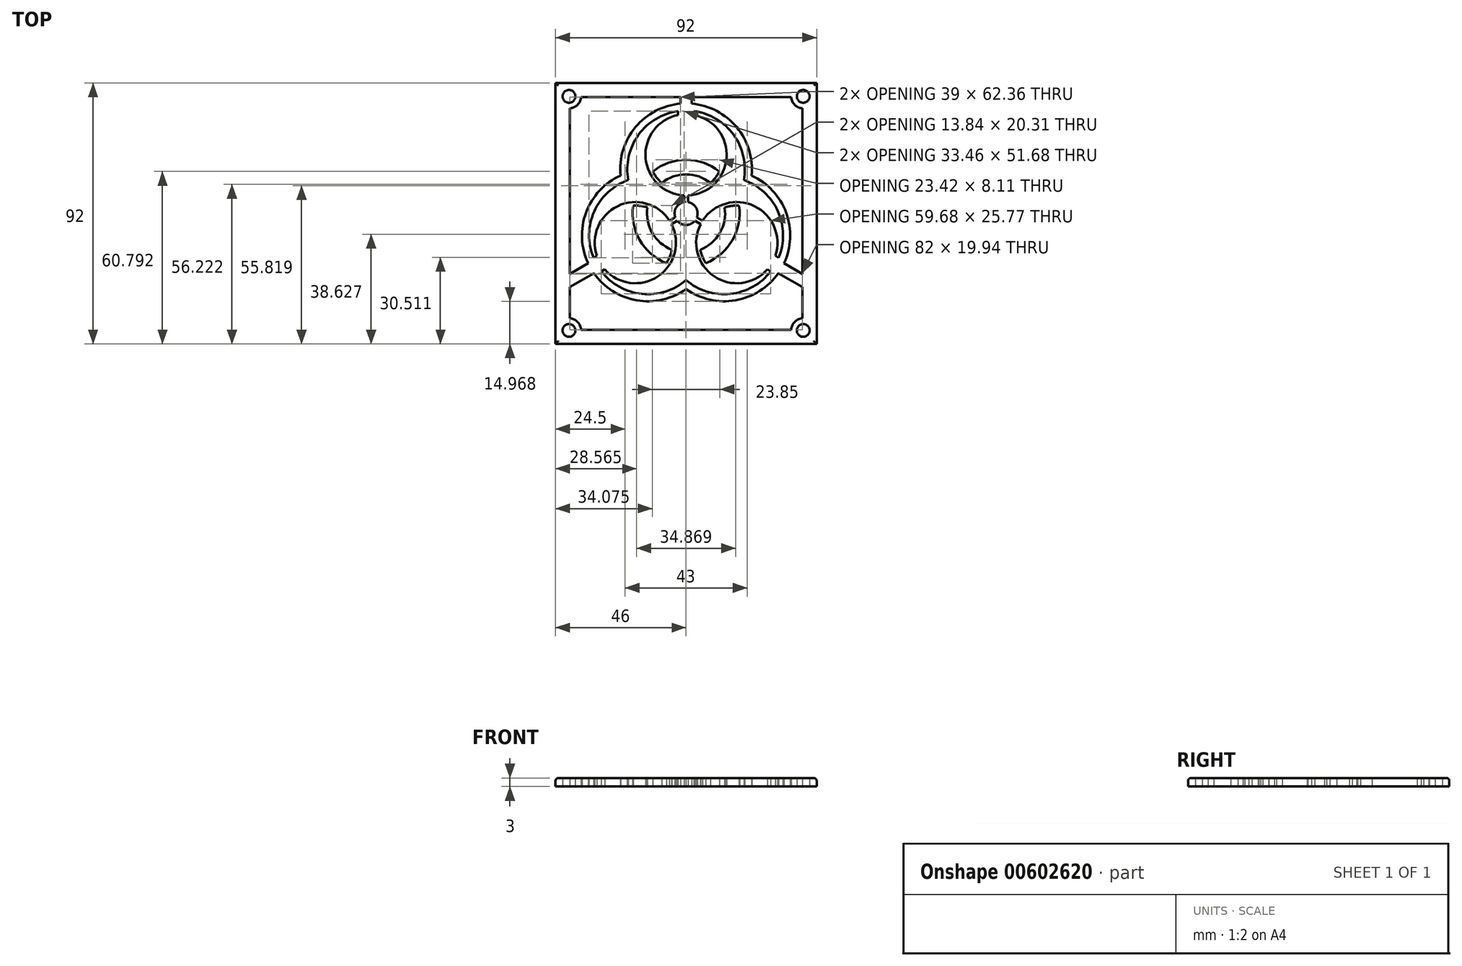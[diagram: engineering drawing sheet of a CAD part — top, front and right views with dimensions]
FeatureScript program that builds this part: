
annotation { "Feature Type Name" : "Feature", "Feature Type Description" : "" }
export const myFeature = defineFeature(function(context is Context, id is Id, definition is map)
    precondition{}
    {
        {
            var Q0;
            Q0=qCreatedBy(makeId("Top.planeOp"),FACE);
            var sketch = newSketch(context, id + "F0", { "sketchPlane" : qUnion([Q0])});
            skPoint(sketch, "E0.middle", {"position": v(0, 0) * mm});
            skLineSegment(sketch, "E1.bottom", {"start": v(46, 46) * mm, "end": v(-46, 46) * mm});
            skLineSegment(sketch, "E1.top", {"start": v(46, -46) * mm, "end": v(-46, -46) * mm});
            skLineSegment(sketch, "E1.left", {"start": v(46, 46) * mm, "end": v(46, -46) * mm});
            skLineSegment(sketch, "E1.right", {"start": v(-46, 46) * mm, "end": v(-46, -46) * mm});
            skCircle(sketch, "E2", {"center": v(-41.25, 41.25) * mm, "radius": 2.25 * mm});
            skCircle(sketch, "E3", {"center": v(41.25, 41.25) * mm, "radius": 2.25 * mm});
            skCircle(sketch, "E4", {"center": v(-41.25, -41.25) * mm, "radius": 2.25 * mm});
            skCircle(sketch, "E5", {"center": v(41.25, -41.25) * mm, "radius": 2.25 * mm});
            skArc(sketch, "E6", {"start": v(-0.7, 4) * mm, "mid": v(-3.51, 2.03) * mm, "end": v(-3.8, -1.39) * mm});
            skArc(sketch, "E7", {"start": v(0.7, 6.34) * mm, "mid": v(14.26, 19.58) * mm, "end": v(2.79, 34.66) * mm});
            skArc(sketch, "E8.1.0", {"start": v(-5.84, -2.56) * mm, "mid": v(-24.09, 2.57) * mm, "end": v(-31.4, -14.91) * mm});
            skArc(sketch, "E8.2.0", {"start": v(5.14, -3.78) * mm, "mid": v(9.82, -22.14) * mm, "end": v(28.62, -19.74) * mm});
            skArc(sketch, "E9", {"start": v(11.71, 14.77) * mm, "mid": v(0, 18.85) * mm, "end": v(-11.71, 14.77) * mm});
            skArc(sketch, "E10", {"start": v(8.58, 10.74) * mm, "mid": v(0, 13.75) * mm, "end": v(-8.58, 10.74) * mm});
            skArc(sketch, "E11.trimOffspring", {"start": v(-20.35, 11.75) * mm, "mid": v(-32.36, 0.7) * mm, "end": v(-32.63, -15.62) * mm});
            skArc(sketch, "E12.trimOffspring", {"start": v(20.35, 11.75) * mm, "mid": v(16.78, 27.67) * mm, "end": v(2.79, 36.06) * mm});
            skArc(sketch, "E13.trimOffspring", {"start": v(-18.65, 2.76) * mm, "mid": v(-16.32, -9.42) * mm, "end": v(-6.93, -17.53) * mm});
            skArc(sketch, "E14.trimOffspring", {"start": v(-13.59, 2.07) * mm, "mid": v(-11.9, -6.87) * mm, "end": v(-5, -12.8) * mm});
            skArc(sketch, "E15.trimOffspring", {"start": v(0, -23.5) * mm, "mid": v(15.57, -28.37) * mm, "end": v(29.84, -20.45) * mm});
            skArc(sketch, "E16.trimOffspring", {"start": v(6.93, -17.53) * mm, "mid": v(16.32, -9.42) * mm, "end": v(18.65, 2.76) * mm});
            skArc(sketch, "E17.trimOffspring", {"start": v(5, -12.8) * mm, "mid": v(11.9, -6.87) * mm, "end": v(13.59, 2.07) * mm});
            skArc(sketch, "E18.0", {"start": v(-11.71, 14.77) * mm, "mid": v(-10.35, 12.6) * mm, "end": v(-8.58, 10.74) * mm});
            skArc(sketch, "E19.1.0", {"start": v(-13.59, 2.07) * mm, "mid": v(-16.08, 2.66) * mm, "end": v(-18.65, 2.76) * mm});
            skArc(sketch, "E19.2.0", {"start": v(5, -12.8) * mm, "mid": v(5.74, -15.26) * mm, "end": v(6.93, -17.53) * mm});
            skArc(sketch, "E20.trimOffspring", {"start": v(8.58, 10.74) * mm, "mid": v(10.35, 12.6) * mm, "end": v(11.71, 14.77) * mm});
            skArc(sketch, "E21.trimOffspring", {"start": v(18.65, 2.76) * mm, "mid": v(16.08, 2.66) * mm, "end": v(13.59, 2.07) * mm});
            skArc(sketch, "E22.trimOffspring", {"start": v(-6.93, -17.53) * mm, "mid": v(-5.74, -15.26) * mm, "end": v(-5, -12.8) * mm});
            skLineSegment(sketch, "E23.left", {"start": v(-0.7, 6.34) * mm, "end": v(-0.7, 4) * mm});
            skLineSegment(sketch, "E23.right", {"start": v(0.7, 6.34) * mm, "end": v(0.7, 4) * mm});
            skLineSegment(sketch, "E24.left", {"start": v(-2.79, 36.06) * mm, "end": v(-2.79, 34.66) * mm});
            skLineSegment(sketch, "E24.right", {"start": v(2.79, 36.06) * mm, "end": v(2.79, 34.66) * mm});
            skArc(sketch, "E25.trimOffspring", {"start": v(-2.79, 36.06) * mm, "mid": v(-16.78, 27.67) * mm, "end": v(-20.35, 11.75) * mm});
            skArc(sketch, "E26.trimOffspring", {"start": v(-2.79, 34.66) * mm, "mid": v(-14.26, 19.58) * mm, "end": v(-0.7, 6.34) * mm});
            skLineSegment(sketch, "E27.1.0", {"start": v(-29.84, -20.45) * mm, "end": v(-28.62, -19.74) * mm});
            skLineSegment(sketch, "E27.1.1", {"start": v(-32.63, -15.62) * mm, "end": v(-31.4, -14.91) * mm});
            skLineSegment(sketch, "E27.1.2", {"start": v(-5.14, -3.78) * mm, "end": v(-3.1, -2.6) * mm});
            skLineSegment(sketch, "E27.1.3", {"start": v(-5.84, -2.56) * mm, "end": v(-3.8, -1.39) * mm});
            skLineSegment(sketch, "E27.2.0", {"start": v(32.63, -15.62) * mm, "end": v(31.4, -14.91) * mm});
            skLineSegment(sketch, "E27.2.1", {"start": v(29.84, -20.45) * mm, "end": v(28.62, -19.74) * mm});
            skLineSegment(sketch, "E27.2.2", {"start": v(5.84, -2.56) * mm, "end": v(3.8, -1.39) * mm});
            skLineSegment(sketch, "E27.2.3", {"start": v(5.14, -3.78) * mm, "end": v(3.1, -2.6) * mm});
            skArc(sketch, "E28.trimOffspring", {"start": v(3.8, -1.39) * mm, "mid": v(3.51, 2.03) * mm, "end": v(0.7, 4) * mm});
            skArc(sketch, "E29.trimOffspring", {"start": v(-3.1, -2.6) * mm, "mid": v(0, -4.05) * mm, "end": v(3.1, -2.6) * mm});
            skArc(sketch, "E30.trimOffspring", {"start": v(32.63, -15.62) * mm, "mid": v(32.36, 0.7) * mm, "end": v(20.35, 11.75) * mm});
            skArc(sketch, "E31.trimOffspring", {"start": v(31.4, -14.91) * mm, "mid": v(24.09, 2.57) * mm, "end": v(5.84, -2.56) * mm});
            skArc(sketch, "E32.trimOffspring", {"start": v(-29.84, -20.45) * mm, "mid": v(-15.57, -28.37) * mm, "end": v(0, -23.5) * mm});
            skArc(sketch, "E33.trimOffspring", {"start": v(-28.62, -19.74) * mm, "mid": v(-9.82, -22.14) * mm, "end": v(-5.14, -3.78) * mm});
            skArc(sketch, "E34.0", {"start": v(-3.12, 38.54) * mm, "mid": v(-18.19, 29.96) * mm, "end": v(-23.1, 13.34) * mm});
            skArc(sketch, "E35.0", {"start": v(-23.1, 13.34) * mm, "mid": v(-35.24, 0.24) * mm, "end": v(-34.49, -17.6) * mm});
            skArc(sketch, "E36.0", {"start": v(-31.82, -21.98) * mm, "mid": v(-16.85, -30.73) * mm, "end": v(0, -26.67) * mm});
            skArc(sketch, "E37.0", {"start": v(0, -26.67) * mm, "mid": v(17.41, -30.64) * mm, "end": v(32.49, -21.06) * mm});
            skArc(sketch, "E38.0", {"start": v(34.94, -16.56) * mm, "mid": v(35.04, 0.77) * mm, "end": v(23.1, 13.34) * mm});
            skArc(sketch, "E39.0", {"start": v(23.1, 13.34) * mm, "mid": v(17.83, 30.4) * mm, "end": v(2, 38.67) * mm});
            skLineSegment(sketch, "E40.1", {"start": v(41, 37) * mm, "end": v(41, -21.36) * mm});
            skLineSegment(sketch, "E40.2", {"start": v(41, -41) * mm, "end": v(39.01, -41) * mm});
            skLineSegment(sketch, "E40.3", {"start": v(-41, 39.01) * mm, "end": v(-41, -21.36) * mm});
            skArc(sketch, "E41.0", {"start": v(-41, 37) * mm, "mid": v(-38.24, 38.24) * mm, "end": v(-37, 41) * mm});
            skArc(sketch, "E42.1.0", {"start": v(-37, -41) * mm, "mid": v(-38.24, -38.24) * mm, "end": v(-41, -37) * mm});
            skArc(sketch, "E42.2.0", {"start": v(41, -37) * mm, "mid": v(38.24, -38.24) * mm, "end": v(37, -41) * mm});
            skArc(sketch, "E42.3.0", {"start": v(37, 41) * mm, "mid": v(38.24, 38.24) * mm, "end": v(41, 37) * mm});
            skLineSegment(sketch, "E43.trimOffspring", {"start": v(37, 41) * mm, "end": v(2, 41) * mm});
            skLineSegment(sketch, "E44.trimOffspring", {"start": v(37, -41) * mm, "end": v(-37, -41) * mm});
            skLineSegment(sketch, "E45.0", {"start": v(-2, 38.67) * mm, "end": v(-2, 41) * mm});
            skLineSegment(sketch, "E46.0", {"start": v(2, 38.67) * mm, "end": v(2, 41) * mm});
            skLineSegment(sketch, "E47.trimOffspring", {"start": v(-2, 41) * mm, "end": v(-37, 41) * mm});
            skArc(sketch, "E48.trimOffspring", {"start": v(-2, 38.67) * mm, "mid": v(-2.56, 38.61) * mm, "end": v(-3.12, 38.54) * mm});
            skLineSegment(sketch, "E49.1.0", {"start": v(-34.49, -17.6) * mm, "end": v(-41, -21.36) * mm});
            skLineSegment(sketch, "E49.1.1", {"start": v(-32.49, -21.06) * mm, "end": v(-41, -25.98) * mm});
            skLineSegment(sketch, "E49.2.0", {"start": v(32.49, -21.06) * mm, "end": v(41, -25.98) * mm});
            skLineSegment(sketch, "E49.2.1", {"start": v(34.49, -17.6) * mm, "end": v(41, -21.36) * mm});
            skPoint(sketch, "E50.orphan", {"position": v(-36.5, -18.77) * mm});
            skPoint(sketch, "E51.orphan", {"position": v(-34.5, -22.23) * mm});
            skPoint(sketch, "E52.orphan", {"position": v(36.5, -18.77) * mm});
            skPoint(sketch, "E53.orphan", {"position": v(34.5, -22.23) * mm});
            skArc(sketch, "E54.trimOffspring", {"start": v(34.49, -17.6) * mm, "mid": v(34.72, -17.09) * mm, "end": v(34.94, -16.56) * mm});
            skLineSegment(sketch, "E55.trimOffspring", {"start": v(41, -25.98) * mm, "end": v(41, -37) * mm});
            skLineSegment(sketch, "E56.trimOffspring", {"start": v(-41, -25.98) * mm, "end": v(-41, -37) * mm});
            skArc(sketch, "E57.trimOffspring", {"start": v(-32.49, -21.06) * mm, "mid": v(-32.16, -21.52) * mm, "end": v(-31.82, -21.98) * mm});
            skSolve(sketch);
        }
        {
            var Q0;
            Q0=makeQuery(id+"F0.imprint","IMPRINT",FACE,{"disambiguationData":[TD([[makeQuery(id+"F0.imprint","IMPRINT",EDGE,{"derivedFrom":sQuery(id+"F0.wireOp",EDGE,"E1.bottom")}),1.0]])]});
            var Q1;
            Q1=makeQuery(id+"F0.imprint","IMPRINT",FACE,{"disambiguationData":[TD([[makeQuery(id+"F0.imprint","IMPRINT",EDGE,{"derivedFrom":sQuery(id+"F0.wireOp",EDGE,"E6")}),1.0]])]});
            extrude(context, id + "F1", {"entities" : qUnion([Q0, Q1]), "depth" : 3 * mm, "offsetDistance" : 25 * mm});
        }
        {
            var Q0;
            Q0=makeQuery(id+"F1.opExtrude","CAP_EDGE",EDGE,{"disambiguationData":[OSD([sQuery(id+"F0.wireOp",EDGE,"E1.bottom")])],"isStart":false});
            var Q1;
            Q1=makeQuery(id+"F1.opExtrude","CAP_EDGE",EDGE,{"disambiguationData":[OSD([sQuery(id+"F0.wireOp",EDGE,"E1.left")])],"isStart":false});
            var Q2;
            Q2=makeQuery(id+"F1.opExtrude","CAP_EDGE",EDGE,{"disambiguationData":[OSD([sQuery(id+"F0.wireOp",EDGE,"E1.right")])],"isStart":false});
            var Q3;
            Q3=makeQuery(id+"F1.opExtrude","CAP_EDGE",EDGE,{"disambiguationData":[OSD([sQuery(id+"F0.wireOp",EDGE,"E1.top")])],"isStart":false});
            fillet(context, id + "F2", {"entities" : qUnion([Q0, Q1, Q2, Q3]), "radius" : 1 * mm, "tangentPropagation" : true, "allowEdgeOverflow" : false});
        }
    });
